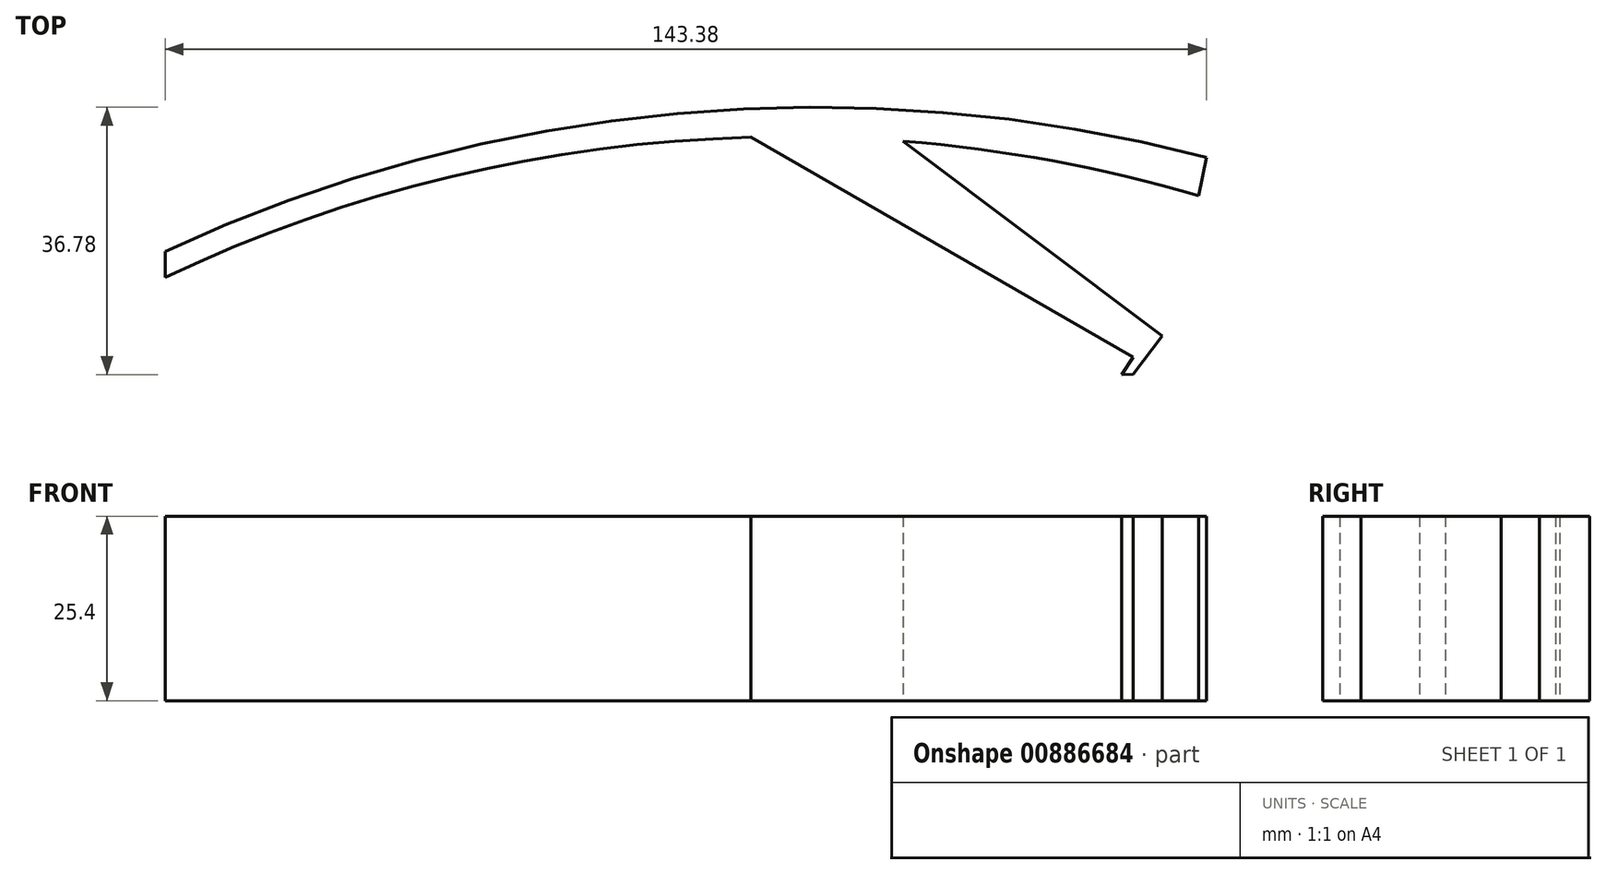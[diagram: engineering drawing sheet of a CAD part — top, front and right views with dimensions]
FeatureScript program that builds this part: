
annotation { "Feature Type Name" : "Feature", "Feature Type Description" : "" }
export const myFeature = defineFeature(function(context is Context, id is Id, definition is map)
    precondition{}
    {
        {
            var Q0;
            Q0=qCreatedBy(makeId("Top.planeOp"),FACE);
            var sketch = newSketch(context, id + "F0", { "sketchPlane" : qUnion([Q0])});
            skArc(sketch, "E0", {"start": v(66.53, 16.53) * mm, "mid": v(-6.3, 22.56) * mm, "end": v(-76.85, 3.57) * mm});
            skArc(sketch, "E1", {"start": v(65.47, 11.24) * mm, "mid": v(-6.73, 18.74) * mm, "end": v(-76.85, 0) * mm});
            skLineSegment(sketch, "E2", {"start": v(-76.85, 3.57) * mm, "end": v(-76.85, 0) * mm});
            skLineSegment(sketch, "E3", {"start": v(66.53, 16.53) * mm, "end": v(65.47, 11.24) * mm});
            skLineSegment(sketch, "E4", {"start": v(24.8, 18.74) * mm, "end": v(60.45, -8.07) * mm});
            skPoint(sketch, "E4.startSnap0", {"position": v(-6.73, 18.74) * mm});
            skLineSegment(sketch, "E5", {"start": v(3.81, 19.3) * mm, "end": v(56.48, -10.98) * mm});
            skLineSegment(sketch, "E6", {"start": v(60.45, -8.07) * mm, "end": v(56.48, -13.35) * mm});
            skLineSegment(sketch, "E7", {"start": v(54.9, -13.36) * mm, "end": v(56.48, -10.98) * mm});
            skLineSegment(sketch, "E8", {"start": v(54.9, -13.36) * mm, "end": v(55.4, -12.6) * mm});
            skLineSegment(sketch, "E9", {"start": v(56.48, -13.35) * mm, "end": v(54.9, -13.36) * mm});
            skSolve(sketch);
        }
        {
            var Q0;
            Q0 = qSketchRegion(id + "F0", true);
            extrude(context, id + "F1", {"entities" : qUnion([Q0]), "depth" : 25.4 * mm, "offsetDistance" : 25.4 * mm});
        }
    });
